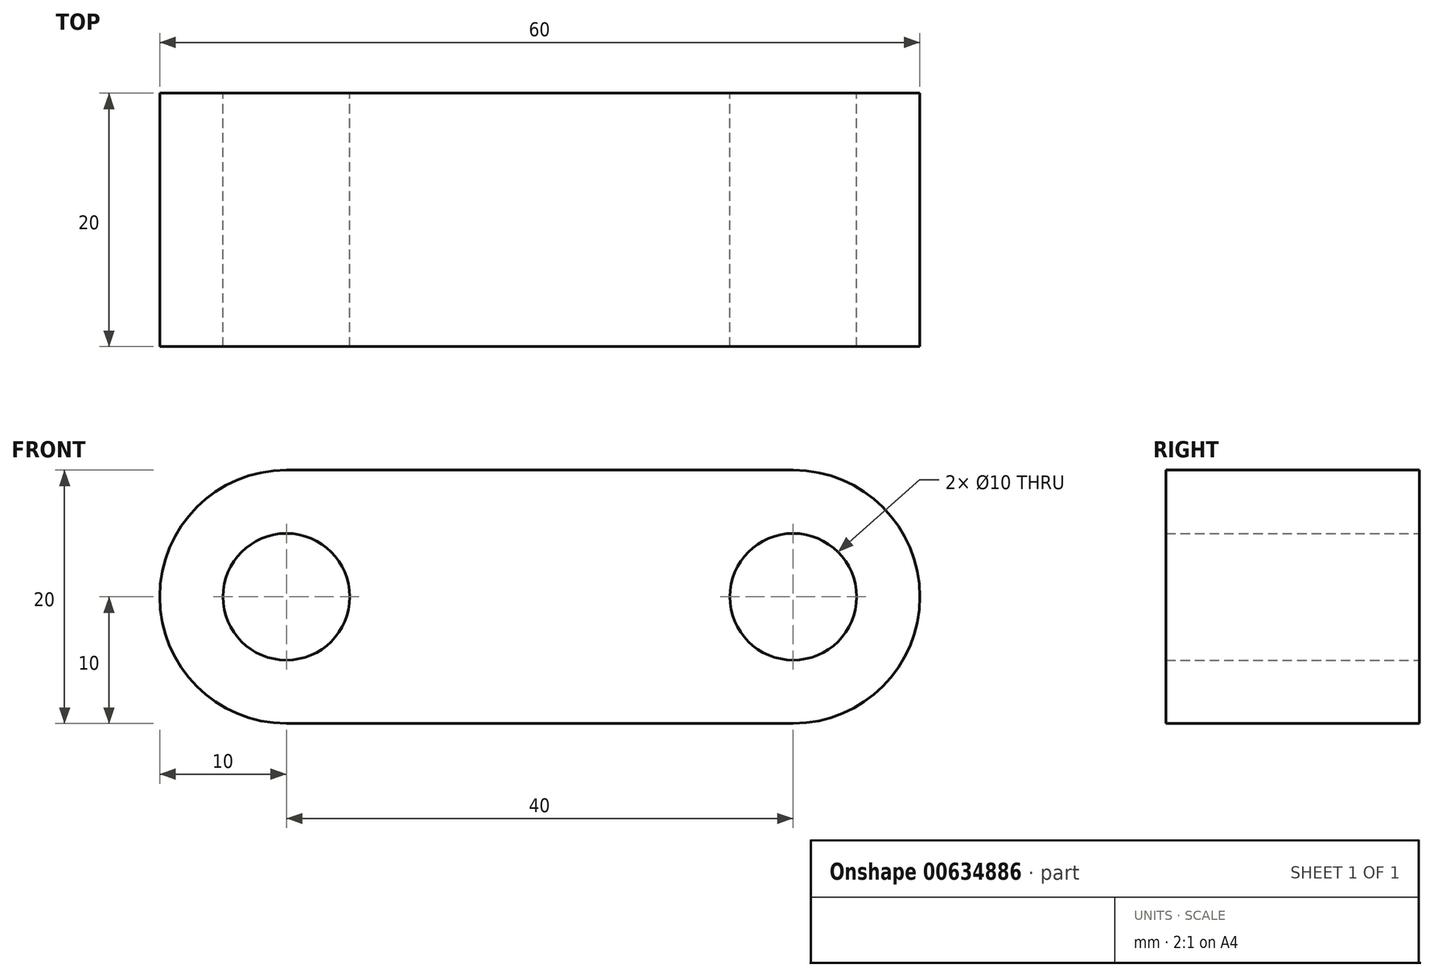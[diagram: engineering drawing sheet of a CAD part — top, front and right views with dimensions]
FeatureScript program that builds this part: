
annotation { "Feature Type Name" : "Feature", "Feature Type Description" : "" }
export const myFeature = defineFeature(function(context is Context, id is Id, definition is map)
    precondition{}
    {
        {
            var Q0;
            Q0=qCreatedBy(makeId("Front.planeOp"),FACE);
            var sketch = newSketch(context, id + "F0", { "sketchPlane" : qUnion([Q0])});
            skLineSegment(sketch, "E0.bottom", {"start": v(0, 0) * mm, "end": v(40, 0) * mm});
            skLineSegment(sketch, "E0.top", {"start": v(0, 20) * mm, "end": v(40, 20) * mm});
            skLineSegment(sketch, "E0.left", {"start": v(0, 0) * mm, "end": v(0, 20) * mm});
            skLineSegment(sketch, "E0.right", {"start": v(40, 0) * mm, "end": v(40, 20) * mm});
            skArc(sketch, "E1", {"start": v(0, 0) * mm, "mid": v(-10, 10) * mm, "end": v(0, 20) * mm});
            skArc(sketch, "E2", {"start": v(40, 0) * mm, "mid": v(50, 10) * mm, "end": v(40, 20) * mm});
            skCircle(sketch, "E3", {"center": v(0, 10) * mm, "radius": 5 * mm});
            skCircle(sketch, "E4", {"center": v(40, 10) * mm, "radius": 5 * mm});
            skSolve(sketch);
        }
        {
            var Q0;
            Q0 = qSketchRegion(id + "F0", true);
            extrude(context, id + "F1", {"entities" : qUnion([Q0]), "depth" : 20 * mm, "offsetDistance" : 25 * mm});
        }
    });
